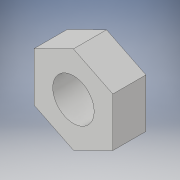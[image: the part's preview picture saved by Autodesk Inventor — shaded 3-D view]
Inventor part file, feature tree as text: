
AUTODESK INVENTOR PART (.ipt)
format: ipt  version: 2018 (Build 220112000, 112)  size: 98,816 bytes
history: native  units: in
note: dims shown in document units (in); Inventor stores cm internally (conversion verified against a paired STEP export)
features: extrude x1, sketch x1
ambient origin geometry x8: Origin, YZ Plane, XZ Plane, XY Plane, X Axis, Y Axis, Z Axis, Center Point
bodies: Solid1 (feature_tree)
feature tree (2):
  extrude  "Extrusion1"  Depth=0.374in
  sketch  "Sketch1"  dims[d2=0.1575in d3=0.0in d6=0.1969in d8=0.374in]
